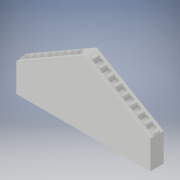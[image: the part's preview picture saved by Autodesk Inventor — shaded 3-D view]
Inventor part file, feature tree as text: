
AUTODESK INVENTOR PART (.ipt)
format: ipt  version: 2017 (Build 210142000, 142)  size: 362,496 bytes
history: native  units: in
note: dims shown in document units (in); Inventor stores cm internally (conversion verified against a paired STEP export)
features: extrude x3, sketch x2
ambient origin geometry x8: Origin, YZ Plane, XZ Plane, XY Plane, X Axis, Y Axis, Z Axis, Center Point
bodies: Solid1 (feature_tree)
feature tree (5):
  extrude  "door"  Depth=100.0in
  sketch  "Sketch3"  dims[d72=21.1325in d73=50.0in d143=10.0in d144=0.0in d282=1.0in d283=1.0in d284=1.5in d285=1.5in d350=1.5in d351=1.0in d352=1.5in d353=0.9496in d356=0.9496in d358=1.0in d359=1.0in d360=1.0in d361=1.5in d362=1.5in d363=1.5in d364=1.0in d365=1.5in d366=0.9496in d367=0.9496in d368=1.0in d369=1.0in d370=1.0in d371=1.5in d372=1.5in d373=1.5in d374=1.0in d375=1.5in d376=0.9496in d377=0.9496in d378=1.0in d379=1.0in d380=1.0in d381=1.5in d382=1.5in d383=1.5in d384=1.0in d385=1.5in d386=0.9496in d387=0.9496in d388=1.0in d389=1.0in d390=1.0in d391=1.5in d392=1.5in d393=1.5in d394=1.0in d395=1.5in d396=0.9496in d397=0.9496in d398=1.0in d399=1.0in d400=1.0in d401=1.5in d402=1.5in d403=1.5in d404=1.0in d405=1.5in d406=0.9496in d407=0.9496in d408=1.0in d409=1.0in d410=1.0in d411=1.5in d412=1.5in d413=1.5in d414=1.0in d415=1.5in d416=0.9496in d417=0.9496in d418=1.0in d419=1.0in d420=1.0in d421=1.5in d422=1.5in d423=1.5in d424=1.0in d425=1.5in d426=0.9496in d427=0.9496in d428=1.0in d429=1.0in d430=1.0in d431=1.5in d432=1.5in d436=0.9496in d439=5.0in d440=0.0in d441=5.0in d442=0.0in]
  extrude  "connection give"  Depth=5.0in
  extrude  "connection receive"  Depth=10.0in TaperAngle=0.0deg
  sketch  "Sketch1"  dims[d70=21.1325in d71=100.0in]
